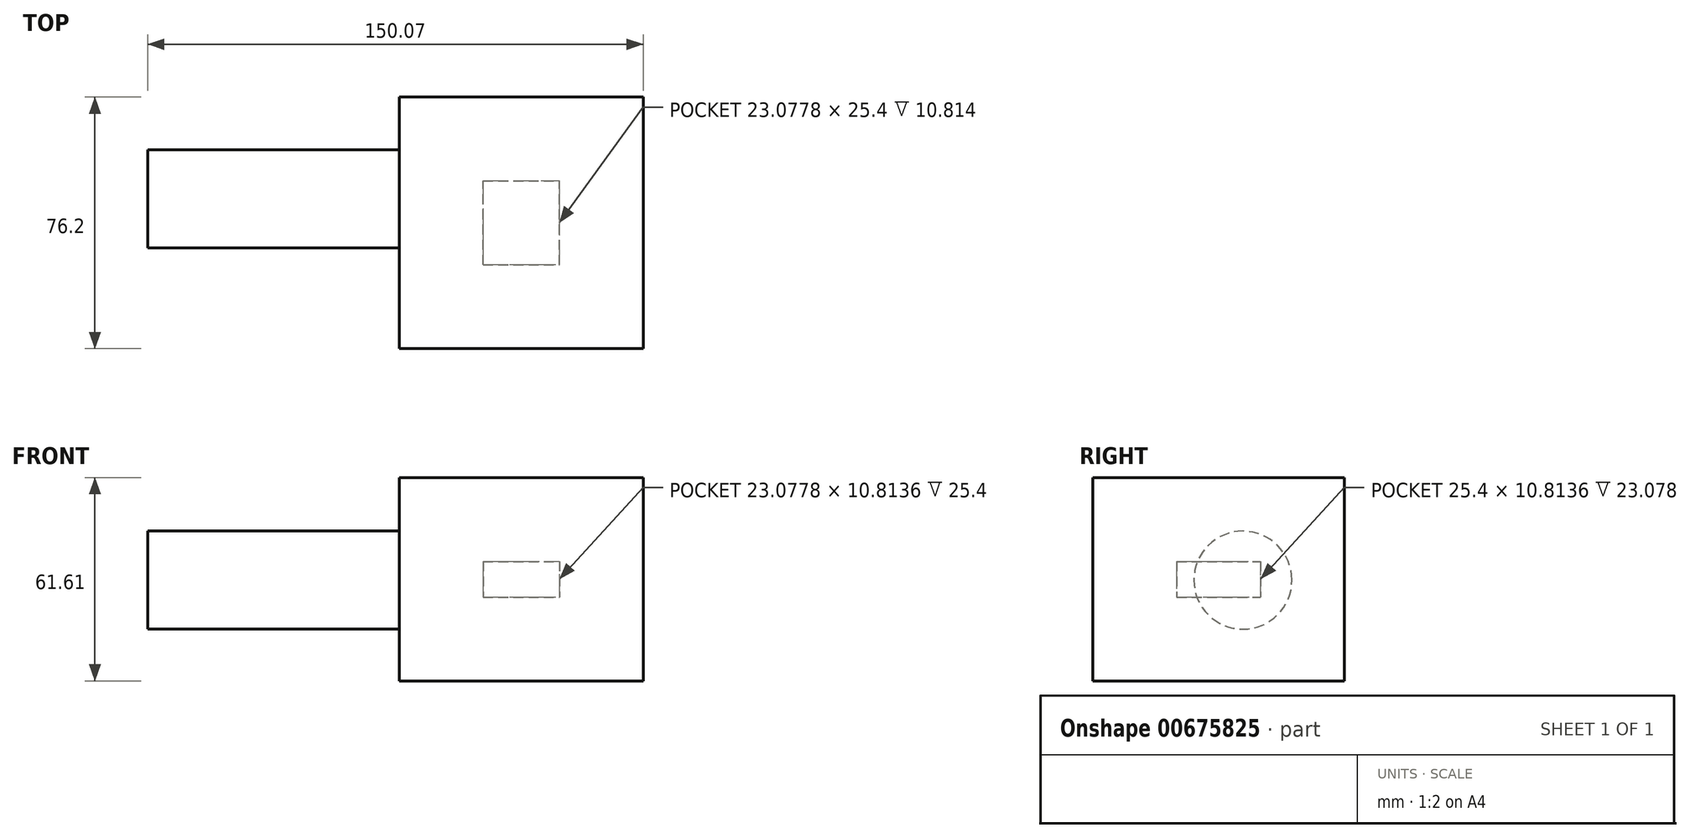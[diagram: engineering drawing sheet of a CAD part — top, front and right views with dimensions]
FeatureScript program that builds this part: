
annotation { "Feature Type Name" : "Feature", "Feature Type Description" : "" }
export const myFeature = defineFeature(function(context is Context, id is Id, definition is map)
    precondition{}
    {
        {
            var Q0;
            Q0=qCreatedBy(makeId("Front.planeOp"),FACE);
            var sketch = newSketch(context, id + "F0", { "sketchPlane" : qUnion([Q0])});
            skLineSegment(sketch, "E0.bottom", {"start": v(-37.81, 31.1) * mm, "end": v(36.06, 31.1) * mm});
            skLineSegment(sketch, "E0.top", {"start": v(-37.81, -30.51) * mm, "end": v(36.06, -30.51) * mm});
            skLineSegment(sketch, "E0.left", {"start": v(-37.81, 31.1) * mm, "end": v(-37.81, -30.51) * mm});
            skLineSegment(sketch, "E0.right", {"start": v(36.06, 31.1) * mm, "end": v(36.06, -30.51) * mm});
            skSolve(sketch);
        }
        {
            var Q0;
            Q0=makeQuery(id+"F0.imprint","IMPRINT",FACE,{"disambiguationData":[TD([[makeQuery(id+"F0.imprint","IMPRINT",EDGE,{"derivedFrom":sQuery(id+"F0.wireOp",EDGE,"E0.bottom")}),-1.0]])]});
            extrude(context, id + "F1", {"entities" : qUnion([Q0]), "endBound" : BoundingType.SYMMETRIC, "depth" : 76.2 * mm, "offsetDistance" : 25.4 * mm});
        }
        {
            var Q0;
            Q0=makeQuery(id+"F1.opExtrude","SWEPT_FACE",FACE,{"disambiguationData":[OSD([sQuery(id+"F0.wireOp",EDGE,"E0.left")])]});
            var sketch = newSketch(context, id + "F2", { "sketchPlane" : qUnion([Q0])});
            skCircle(sketch, "E1", {"center": v(-7.34, 0) * mm, "radius": 14.85 * mm});
            skSolve(sketch);
        }
        {
            var Q0;
            Q0=makeQuery(id+"F2.imprint","IMPRINT",FACE,{"disambiguationData":[TD([[makeQuery(id+"F2.imprint","IMPRINT",EDGE,{"derivedFrom":sQuery(id+"F2.wireOp",EDGE,"E1")}),1.0]])]});
            extrude(context, id + "F3", {"entities" : qUnion([Q0]), "operationType" : NewBodyOperationType.ADD, "depth" : 76.2 * mm, "offsetDistance" : 25.4 * mm});
        }
        {
            var Q0;
            Q0=makeQuery(id+"F3.opExtrude","CAP_FACE",FACE,{"disambiguationData":[OSD([sQuery(id+"F2.wireOp",EDGE,"E1")])],"isStart":false});
            shell(context, id + "F4", {"entities" : qUnion([Q0]), "thickness" : 25.4 * mm});
        }
    });
